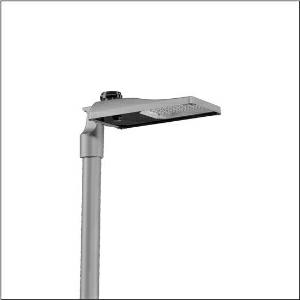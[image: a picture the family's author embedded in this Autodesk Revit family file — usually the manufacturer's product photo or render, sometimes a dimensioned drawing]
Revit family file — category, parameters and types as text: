
# Revit family: streetlight_sl_31_mini___st1_0a_5xh2d35m08ja_015a
name_source: partatom
category: Lighting Fixtures
units: mm (PartAtom-declared; Revit-internal decimal feet)

## family parameters
Cut with Voids When Loaded = No
Host = Face
Light Source = No
Part Type = Normal
Room Calculation Point = No
Round Connector Dimension = Use Diameter
Shared = No

## types (1)
- --- (1 x LED, 12270 lm, 82.5 W, 3000K)
    Apparent Load = 83 VA
    CIE Flux Codes = 40 73 97 100 100
    Color Rendering = 70
    Color Temperature = 3000K
    Default Elevation = 1800 mm
    Description = Streetlight SL 31 mini NEMA (7pin), Desk-Remote mast luminaire for post-top, side-entry; light control with lens of PMMA; light distribution: ST1.0a, direct asymmetric distribution, for standard-compliant lighting for roads and squares; LED: luminous flux: 12.270lm, light colour: 730, colour temperature: 3000K; luminous efficacy: 148,7lm/W; control: pre-setting: linear dimming characteristic, flexible luminous flux parameterisation, time-dependent luminous flux control, constant luminous flux control, intelligent temperature release in ECG and LED module, overheat protection; luminaire housing, of diecast aluminium, SITECO metallic grey (DB 702S), corrosivity category C5 high according to DIN EN ISO 12944; cover of toughened safety glass, transparent, mast flange of diecast aluminium, SITECO metallic grey (DB 702S), spigot size: 76/60mm, mast flange included unmounted; cable length: 10,5m, connection cable pre-assembled; mains connection: 220..240V, AC, 50/60Hz; power consumption (at start of service life): 82,5W / (at end of service life): 90,1W / (with reduced operation 50%): 36,8W; protection rating (complete): IP66; insulation class (complete): insulation class I (protective earthing); impact resistance: IK09; certification: CE, ENEC, ENEC+, VDE, UKCA; permissible operating ambient temperature for outdoor applications: -40..+50°C; packaging unit: 1 piece

Light Distribution: ST1.0a
    Height = 76 mm
    Lamp = 1 x LED
    Lamp Light Flux = 12270 lm
    Lamp Power = 82.5 W
    Lamp count = 1
    Length = 547 mm
    Luminous efficacy = 149 lm/W
    Manufacturer = Siteco
    ModVariant = No
    Model = 5XH2D35M08JA
    Number of Poles = 1
    OnlyDefault = Yes
    Power Factor = 1
    Product Name = Streetlight SL 31 mini | ST1.0a
    Product group = mast luminaire | pylon top
    ProductGroupID = 6100
    Protection Class = Protection class I
    Protection Degree = IP 66
    RLX_Detail_Level = 1
    RLX_Emergency_Light_Flux = 0 lm
    RLX_Emergency_Type = 0
    RLX_Emergency_Type_DB = No
    RlxData = <blob elided: 40361 chars, md5=752c657c>
    Socket = socket
    Standby Power = 0 W
    System Light Flux = 12270 lm
    System Power = 83 W
    Type Comments = factory setting: luminous flux: 100 % | dim-lin: 254 | 870 mA
    Type Image = l_1300324.jpg
    URL = http://relux.com
    VarID = @adj_057475
    Voltage = 0 V
    Weight = 0.00 kg
    Width = 265 mm

## geometry (parser evidence)
native form markers: Blend x4, Sweep x10
no freeform markers — native parametric forms only
